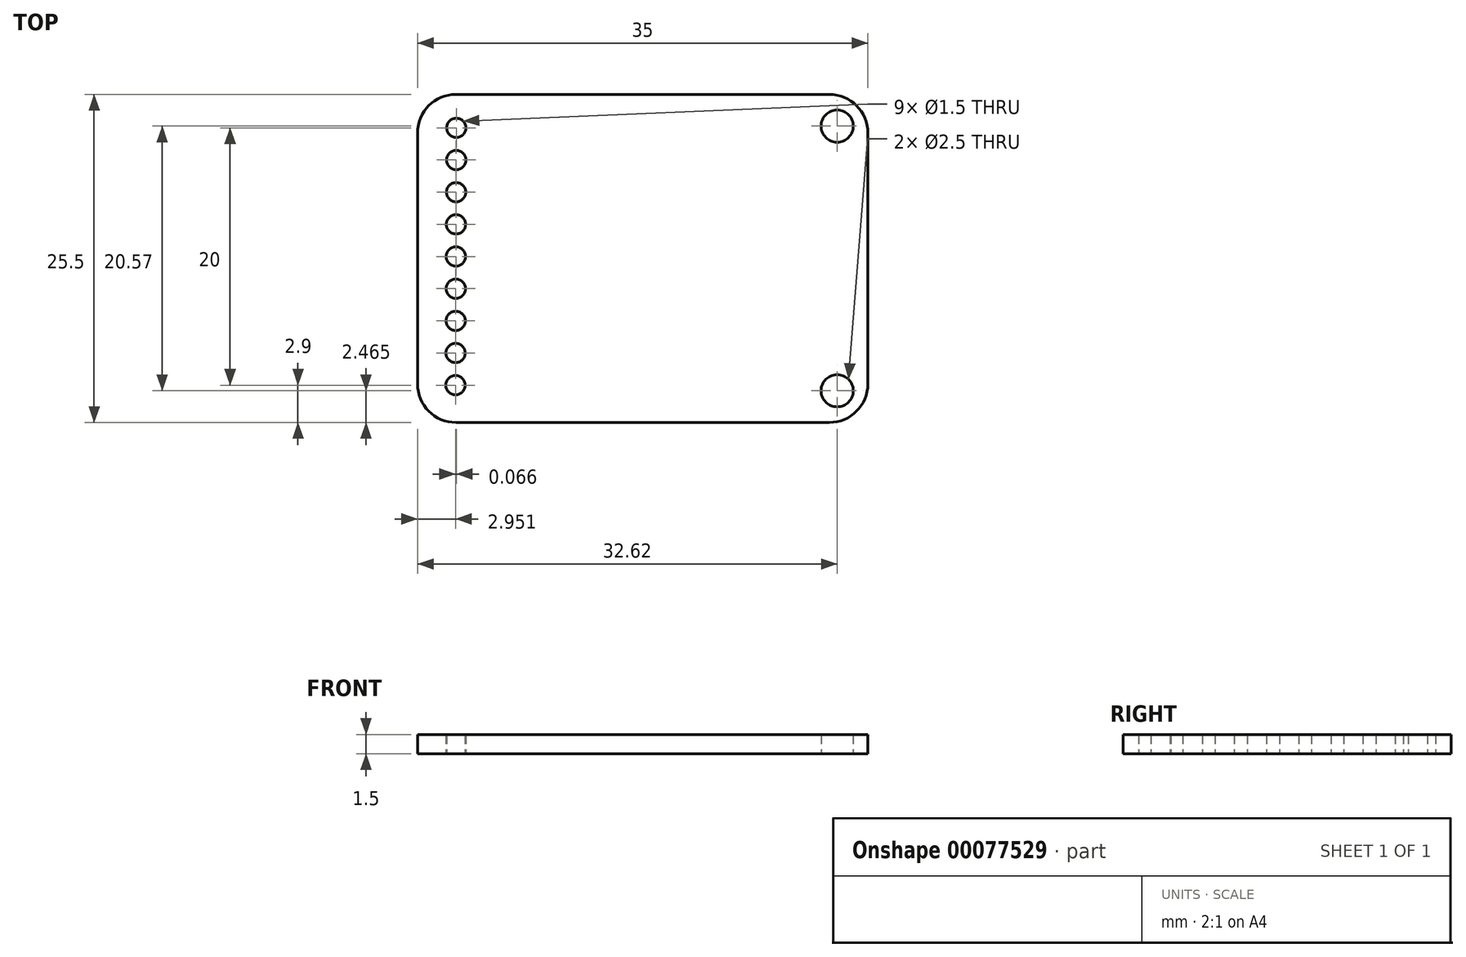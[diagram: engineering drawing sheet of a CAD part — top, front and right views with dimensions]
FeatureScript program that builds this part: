
annotation { "Feature Type Name" : "Feature", "Feature Type Description" : "" }
export const myFeature = defineFeature(function(context is Context, id is Id, definition is map)
    precondition{}
    {
        {
            var Q0;
            Q0=qCreatedBy(makeId("Top.planeOp"),FACE);
            var sketch = newSketch(context, id + "F0", { "sketchPlane" : qUnion([Q0])});
            skLineSegment(sketch, "E0.bottom", {"start": v(-14.5, 12.75) * mm, "end": v(14.5, 12.75) * mm});
            skLineSegment(sketch, "E0.top", {"start": v(-14.5, -12.75) * mm, "end": v(14.5, -12.75) * mm});
            skLineSegment(sketch, "E0.left", {"start": v(-17.5, 9.75) * mm, "end": v(-17.5, -9.75) * mm});
            skLineSegment(sketch, "E0.right", {"start": v(17.5, 9.75) * mm, "end": v(17.5, -9.75) * mm});
            skPoint(sketch, "E0.middle", {"position": v(0, 0) * mm});
            skLineSegment(sketch, "E1.bottom", {"start": v(-7.78, 8.54) * mm, "end": v(7.78, 8.54) * mm});
            skLineSegment(sketch, "E1.top", {"start": v(-7.78, -8.54) * mm, "end": v(7.78, -8.54) * mm});
            skLineSegment(sketch, "E1.left", {"start": v(-7.78, 8.54) * mm, "end": v(-7.78, -8.54) * mm});
            skLineSegment(sketch, "E1.right", {"start": v(7.78, 8.54) * mm, "end": v(7.78, -8.54) * mm});
            skLineSegment(sketch, "E2", {"start": v(15.12, 12.75) * mm, "end": v(15.12, -12.75) * mm, "construction": true});
            skLineSegment(sketch, "E3", {"start": v(-14.48, 12.75) * mm, "end": v(-14.48, -12.75) * mm, "construction": true});
            skCircle(sketch, "E4", {"center": v(15.12, 10.28) * mm, "radius": 1.25 * mm});
            skCircle(sketch, "E5", {"center": v(15.12, -10.28) * mm, "radius": 1.25 * mm});
            skCircle(sketch, "E6", {"center": v(-14.48, 10.15) * mm, "radius": 0.75 * mm});
            skCircle(sketch, "E7.1.0.0", {"center": v(-14.5, 7.65) * mm, "radius": 0.75 * mm});
            skLineSegment(sketch, "E7.1.0.1", {"start": v(-14.5, 10.25) * mm, "end": v(-14.5, -15.25) * mm, "construction": true});
            skCircle(sketch, "E7.2.0.0", {"center": v(-14.5, 5.15) * mm, "radius": 0.75 * mm});
            skLineSegment(sketch, "E7.2.0.1", {"start": v(-14.5, 7.75) * mm, "end": v(-14.5, -17.75) * mm, "construction": true});
            skCircle(sketch, "E7.3.0.0", {"center": v(-14.5, 2.65) * mm, "radius": 0.75 * mm});
            skLineSegment(sketch, "E7.3.0.1", {"start": v(-14.5, 5.25) * mm, "end": v(-14.5, -20.25) * mm, "construction": true});
            skCircle(sketch, "E7.4.0.0", {"center": v(-14.52, 0.15) * mm, "radius": 0.75 * mm});
            skLineSegment(sketch, "E7.4.0.1", {"start": v(-14.52, 2.75) * mm, "end": v(-14.52, -22.75) * mm, "construction": true});
            skCircle(sketch, "E7.5.0.0", {"center": v(-14.52, -2.35) * mm, "radius": 0.75 * mm});
            skLineSegment(sketch, "E7.5.0.1", {"start": v(-14.52, 0.25) * mm, "end": v(-14.52, -25.25) * mm, "construction": true});
            skCircle(sketch, "E7.6.0.0", {"center": v(-14.53, -4.85) * mm, "radius": 0.75 * mm});
            skLineSegment(sketch, "E7.6.0.1", {"start": v(-14.53, -2.25) * mm, "end": v(-14.53, -27.75) * mm, "construction": true});
            skCircle(sketch, "E7.7.0.0", {"center": v(-14.54, -7.35) * mm, "radius": 0.75 * mm});
            skLineSegment(sketch, "E7.7.0.1", {"start": v(-14.54, -4.75) * mm, "end": v(-14.54, -30.25) * mm, "construction": true});
            skCircle(sketch, "E7.8.0.0", {"center": v(-14.55, -9.85) * mm, "radius": 0.75 * mm});
            skLineSegment(sketch, "E7.8.0.1", {"start": v(-14.55, -7.25) * mm, "end": v(-14.55, -32.75) * mm, "construction": true});
            skLineSegment(sketch, "E7.direction1", {"start": v(-14.48, 10.15) * mm, "end": v(-14.5, 7.65) * mm, "construction": true});
            skPoint(sketch, "E8.visualSharp", {"position": v(-17.5, 12.75) * mm});
            skArc(sketch, "E8.filletArc", {"start": v(-14.5, 12.75) * mm, "mid": v(-16.62, 11.87) * mm, "end": v(-17.5, 9.75) * mm});
            skPoint(sketch, "E9.visualSharp", {"position": v(17.5, 12.75) * mm});
            skArc(sketch, "E9.filletArc", {"start": v(17.5, 9.75) * mm, "mid": v(16.62, 11.87) * mm, "end": v(14.5, 12.75) * mm});
            skPoint(sketch, "E10.visualSharp", {"position": v(17.5, -12.75) * mm});
            skArc(sketch, "E10.filletArc", {"start": v(14.5, -12.75) * mm, "mid": v(16.62, -11.87) * mm, "end": v(17.5, -9.75) * mm});
            skPoint(sketch, "E11.visualSharp", {"position": v(-17.5, -12.75) * mm});
            skArc(sketch, "E11.filletArc", {"start": v(-17.5, -9.75) * mm, "mid": v(-16.62, -11.87) * mm, "end": v(-14.5, -12.75) * mm});
            skSolve(sketch);
        }
        {
            var Q0;
            Q0 = qSketchRegion(id + "F0", true);
            var Q1;
            Q1=makeQuery(id+"F0.imprint","IMPRINT",FACE,{"disambiguationData":[TD([[makeQuery(id+"F0.imprint","IMPRINT",EDGE,{"derivedFrom":sQuery(id+"F0.wireOp",EDGE,"E0.bottom")}),-1.0]])]});
            var Q2;
            Q2=makeQuery(id+"F0.imprint","IMPRINT",FACE,{"disambiguationData":[TD([[makeQuery(id+"F0.imprint","IMPRINT",EDGE,{"derivedFrom":sQuery(id+"F0.wireOp",EDGE,"E1.bottom")}),-1.0]])]});
            extrude(context, id + "F1", {"entities" : qUnion([Q0, Q1, Q2]), "depth" : 1.5 * mm});
        }
    });
